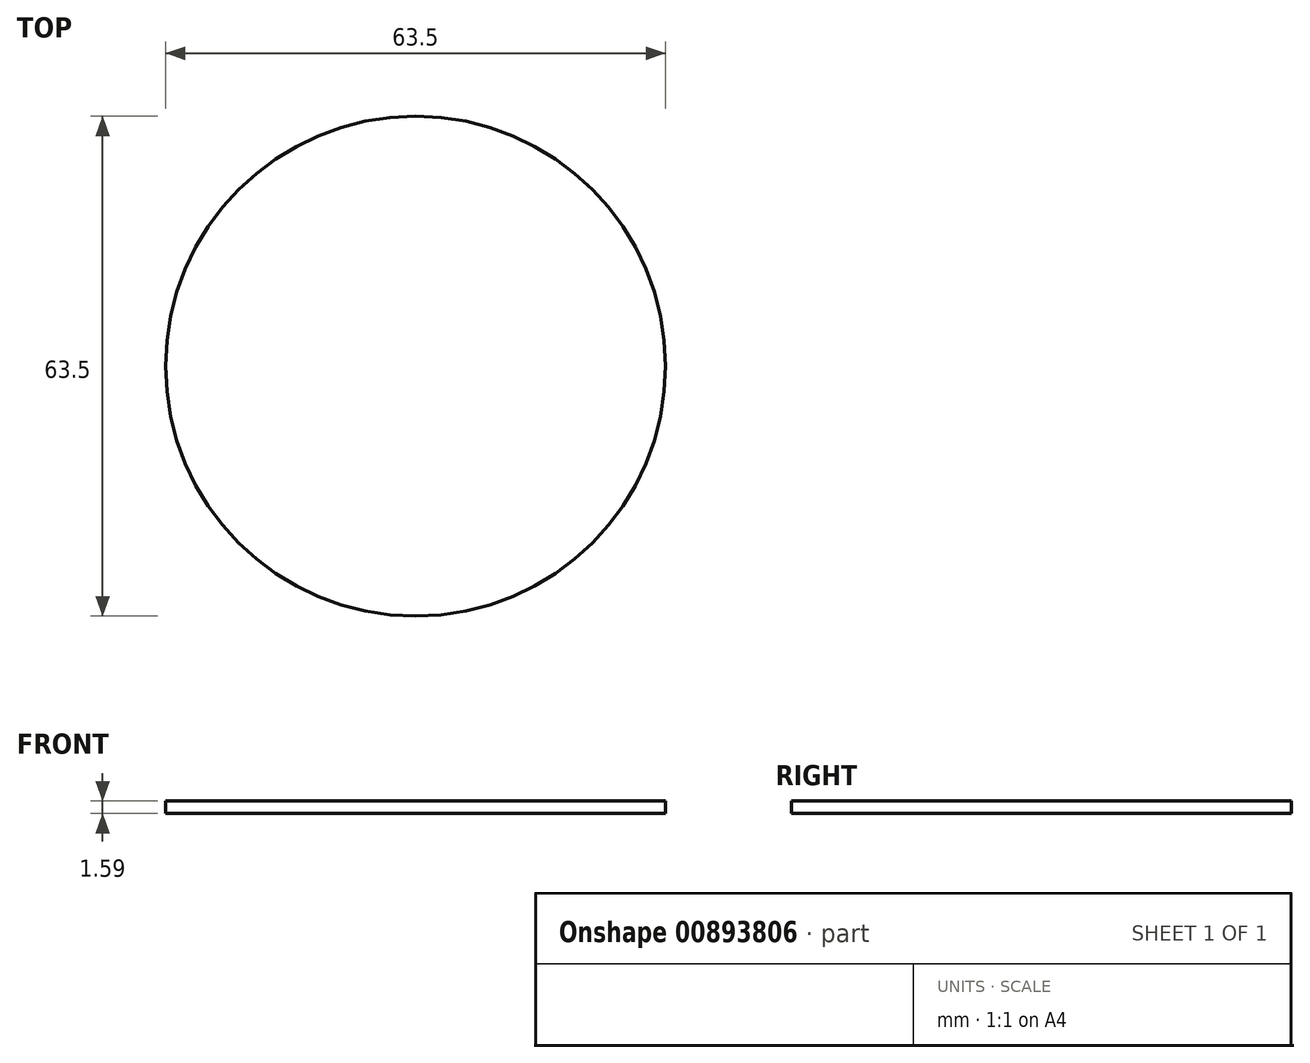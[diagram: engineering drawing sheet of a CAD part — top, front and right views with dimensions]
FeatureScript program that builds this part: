
annotation { "Feature Type Name" : "Feature", "Feature Type Description" : "" }
export const myFeature = defineFeature(function(context is Context, id is Id, definition is map)
    precondition{}
    {
        {
            var Q0;
            Q0=qCreatedBy(makeId("Top.planeOp"),FACE);
            var sketch = newSketch(context, id + "F0", { "sketchPlane" : qUnion([Q0])});
            skCircle(sketch, "E0", {"center": v(0, 0) * mm, "radius": 31.75 * mm});
            skSolve(sketch);
        }
        {
            var Q0;
            Q0 = qSketchRegion(id + "F0", true);
            extrude(context, id + "F1", {"entities" : qUnion([Q0]), "depth" : 1.59 * mm, "offsetDistance" : 25.4 * mm});
        }
    });
